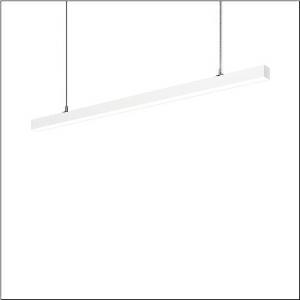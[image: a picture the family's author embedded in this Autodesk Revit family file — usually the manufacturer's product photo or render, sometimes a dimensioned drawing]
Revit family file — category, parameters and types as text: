
# Revit family: silica_21_51mx30db35wb
name_source: partatom
category: Lighting Fixtures
units: mm (PartAtom-declared; Revit-internal decimal feet)

## family parameters
Cut with Voids When Loaded = No
Host = Face
Light Source = No
Part Type = Normal
Room Calculation Point = No
Round Connector Dimension = Use Diameter
Shared = No

## types (1)
- --- (1 x LED, 5260 lm, 34.1 W, 3000K)
    Apparent Load = 34 VA
    CIE Flux Codes = 47 79 96 57 100
    Color Rendering = 80
    Color Temperature = 3000K
    Default Elevation = 1800 mm
    Description = Silica 21, office luminaire, primary optical cover: cover, of PMMA, opal, light emission: direct/indirect distribution, primary light characteristic: symmetric, installation type: suspended mounting, LED, rated luminous flux: 5.260lm, luminous efficacy: 154lm/W, light colour: 830, colour temperature: 3000K, control gear: DALI 2, with terminal, 3+2-pole, max. 2.5mm², mains connection: 220..240V, AC, 50/60Hz, rated input power: 34.1W, luminaire housing, of aluminium, traffic white (RAL 9016), length: 1.504mm, width: 53mm, height: 53mm, protection rating (complete): IP20, insulation class (complete): insulation class I (protective earthing), certification: CE, permissible operating ambient temperature: 0..+35°C, standard: EN 50419, packaging unit: 1 piece
    Height = 53 mm
    Lamp = 1 x LED
    Lamp Light Flux = 5260 lm
    Lamp Power = 34.1 W
    Lamp count = 1
    Length = 1504 mm
    Luminous efficacy = 154 lm/W
    Manufacturer = Siteco
    ModVariant = No
    Model = 51MX30DB35WB
    Mounting Place = Ceiling
    Mounting Type = Pendant
    Number of Poles = 1
    OnlyDefault = Yes
    Power Factor = 1
    Product Name = Silica 21
    Product group = office luminaire | ceiling pendant
    ProductGroupID = 903
    Protection Class = Protection class I
    Protection Degree = IP 20
    RLX_Detail_Level = 1
    RLX_Emergency_Light_Flux = 0 lm
    RLX_Emergency_Type = 0
    RLX_Emergency_Type_DB = No
    RlxData = <blob elided: 18489 chars, md5=8404a949>
    Socket = socket
    Standby Power = 0 W
    System Light Flux = 5260 lm
    System Power = 34 W
    Type Comments = factory setting: luminous flux: 100 % | dim-lin: 254 | 233 mA
    Type Image = l_1349027.jpg
    URL = http://relux.com
    VarID = @adj_117019
    Voltage = 0 V
    Weight = 0.00 kg
    Width = 53 mm

## geometry (parser evidence)
native form markers: Blend x4, Sweep x13
no freeform markers — native parametric forms only
